# Revit family: Cascata Time Power Floor 20201229 connettori OK
name_source: partatom
category: Attrezzatura meccanica
units: mm (PartAtom-declared; Revit-internal decimal feet)

## family parameters
Basato su piano di lavoro = No
Condiviso = No
Numero OmniClass = 23.75.00.00
Punto di calcolo locali = No
Quota connettore circolare = Usa diametro
Sempre verticale = Sì
Taglio con vuoti quando caricato = No
Tipo di parte = Normale
Titolo OmniClass = Climate Control (HVAC)

## types (23) — shared parameters
Condensate Drain (cascade) = 40 mm  [stored 0.131234 ft]
Date of publishing = 07/01/2021
Design country = Italy
Equilibratore_SX = Sì
Gas Inlet Diameter (cascade) = 165 mm
Manufacturer country = Italy
Manufacturer name = Italtherm S.p.a.
Material main = Metal
Material secondary = Plastic
Product family = Heating
Product group = Thermal unit
Vis.Equil.sx = Sì
zero-valued in all types: Edition number, Prospetto di default

## per-type parameters (varying)
- 340 kW_4 Caldaie: Caldaia_0=Time Power Floor : Time Power Floor 90 K; Caldaia_1=Time Power Floor : Time Power Floor 90 K; Caldaia_2=Time Power Floor : Time Power Floor 90 K; Caldaia_3=Time Power Floor : Time Power Floor 90 K; Diam_flange_equilib=210 mm  [stored 0.688976 ft]; Distanza_ki_INAIL=2308 mm  [stored 7.57218 ft]; Equilibratore_DX=No; Flue outlet (cascade)=200 mm  [stored 0.656168 ft]; Hydronic Return Diameter (cascade)=210 mm  [stored 0.688976 ft]; Hydronic Supply Diameter (cascade)=210 mm  [stored 0.688976 ft]; Maximum heating heat input=340.00 kW; NascTubo=5100 mm  [stored 16.7323 ft]; NumeroCaldaie=4; Numero_Caldaie=4; On_FumiDX_Off_FumiSX=Sì; Qn_MAX=340.00 kW; Scambiatore_DX=No; Scambiatore_SX=No; Sottr=2504 mm  [stored 8.21522 ft]; Vis.Equil.dx=No; Vis.FumiDX=Sì; Vis.FumiSX=No; Vis.Scamb.dx=No; Vis.Scamb.sx=No; Vis.scarico3=Sì; Vis.scarico4=Sì; Visibilità_caldaia_2=Sì; Visibilità_caldaia_3=Sì
- 363 kW_4 Caldaie: Caldaia_0=Time Power Floor : Time Power Floor 90 K; Caldaia_1=Time Power Floor : Time Power Floor 90 K; Caldaia_2=Time Power Floor : Time Power Floor 90 K; Caldaia_3=Time Power Floor : Time Power Floor 115 K; Diam_flange_equilib=210 mm  [stored 0.688976 ft]; Distanza_ki_INAIL=2308 mm  [stored 7.57218 ft]; Equilibratore_DX=Sì; Flue outlet (cascade)=200 mm  [stored 0.656168 ft]; Hydronic Return Diameter (cascade)=210 mm  [stored 0.688976 ft]; Hydronic Supply Diameter (cascade)=210 mm  [stored 0.688976 ft]; Maximum heating heat input=363.00 kW; NascTubo=5100 mm  [stored 16.7323 ft]; NumeroCaldaie=4; Numero_Caldaie=4; On_FumiDX_Off_FumiSX=Sì; Qn_MAX=363.00 kW; Scambiatore_DX=Sì; Scambiatore_SX=Sì; Sottr=2504 mm  [stored 8.21522 ft]; Vis.Equil.dx=Sì; Vis.FumiDX=Sì; Vis.FumiSX=No; Vis.Scamb.dx=Sì; Vis.Scamb.sx=Sì; Vis.scarico3=Sì; Vis.scarico4=Sì; Visibilità_caldaia_2=Sì; Visibilità_caldaia_3=Sì
- 386 kW_4 Caldaie: Caldaia_0=Time Power Floor : Time Power Floor 90 K; Caldaia_1=Time Power Floor : Time Power Floor 90 K; Caldaia_2=Time Power Floor : Time Power Floor 115 K; Caldaia_3=Time Power Floor : Time Power Floor 115 K; Diam_flange_equilib=210 mm  [stored 0.688976 ft]; Distanza_ki_INAIL=2308 mm  [stored 7.57218 ft]; Equilibratore_DX=Sì; Flue outlet (cascade)=200 mm  [stored 0.656168 ft]; Hydronic Return Diameter (cascade)=210 mm  [stored 0.688976 ft]; Hydronic Supply Diameter (cascade)=210 mm  [stored 0.688976 ft]; Maximum heating heat input=386.00 kW; NascTubo=5100 mm  [stored 16.7323 ft]; NumeroCaldaie=4; Numero_Caldaie=4; On_FumiDX_Off_FumiSX=Sì; Qn_MAX=386.00 kW; Scambiatore_DX=Sì; Scambiatore_SX=Sì; Sottr=2504 mm  [stored 8.21522 ft]; Vis.Equil.dx=Sì; Vis.FumiDX=Sì; Vis.FumiSX=No; Vis.Scamb.dx=Sì; Vis.Scamb.sx=Sì; Vis.scarico3=Sì; Vis.scarico4=Sì; Visibilità_caldaia_2=Sì; Visibilità_caldaia_3=Sì
- 405 kW_4 Caldaie: Caldaia_0=Time Power Floor : Time Power Floor 160 K; Caldaia_1=Time Power Floor : Time Power Floor 90 K; Caldaia_2=Time Power Floor : Time Power Floor 90 K; Caldaia_3=Time Power Floor : Time Power Floor 90 K; Diam_flange_equilib=210 mm  [stored 0.688976 ft]; Distanza_ki_INAIL=2308 mm  [stored 7.57218 ft]; Equilibratore_DX=Sì; Flue outlet (cascade)=200 mm  [stored 0.656168 ft]; Hydronic Return Diameter (cascade)=210 mm  [stored 0.688976 ft]; Hydronic Supply Diameter (cascade)=210 mm  [stored 0.688976 ft]; Maximum heating heat input=405.00 kW; NascTubo=5100 mm  [stored 16.7323 ft]; NumeroCaldaie=4; Numero_Caldaie=4; On_FumiDX_Off_FumiSX=Sì; Qn_MAX=405.00 kW; Scambiatore_DX=Sì; Scambiatore_SX=Sì; Sottr=2504 mm  [stored 8.21522 ft]; Vis.Equil.dx=Sì; Vis.FumiDX=Sì; Vis.FumiSX=No; Vis.Scamb.dx=Sì; Vis.Scamb.sx=Sì; Vis.scarico3=Sì; Vis.scarico4=Sì; Visibilità_caldaia_2=Sì; Visibilità_caldaia_3=Sì
- 409 kW_4 Caldaie: Caldaia_0=Time Power Floor : Time Power Floor 115 K; Caldaia_1=Time Power Floor : Time Power Floor 115 K; Caldaia_2=Time Power Floor : Time Power Floor 115 K; Caldaia_3=Time Power Floor : Time Power Floor 90 K; Diam_flange_equilib=210 mm  [stored 0.688976 ft]; Distanza_ki_INAIL=2308 mm  [stored 7.57218 ft]; Equilibratore_DX=Sì; Flue outlet (cascade)=200 mm  [stored 0.656168 ft]; Hydronic Return Diameter (cascade)=210 mm  [stored 0.688976 ft]; Hydronic Supply Diameter (cascade)=210 mm  [stored 0.688976 ft]; Maximum heating heat input=409.00 kW; NascTubo=5100 mm  [stored 16.7323 ft]; NumeroCaldaie=4; Numero_Caldaie=4; On_FumiDX_Off_FumiSX=Sì; Qn_MAX=409.00 kW; Scambiatore_DX=Sì; Scambiatore_SX=Sì; Sottr=2504 mm  [stored 8.21522 ft]; Vis.Equil.dx=Sì; Vis.FumiDX=Sì; Vis.FumiSX=No; Vis.Scamb.dx=Sì; Vis.Scamb.sx=Sì; Vis.scarico3=Sì; Vis.scarico4=Sì; Visibilità_caldaia_2=Sì; Visibilità_caldaia_3=Sì
- 428 kW_4 Caldaie: Caldaia_0=Time Power Floor : Time Power Floor 160 K; Caldaia_1=Time Power Floor : Time Power Floor 115 K; Caldaia_2=Time Power Floor : Time Power Floor 90 K; Caldaia_3=Time Power Floor : Time Power Floor 90 K; Diam_flange_equilib=210 mm  [stored 0.688976 ft]; Distanza_ki_INAIL=2308 mm  [stored 7.57218 ft]; Equilibratore_DX=Sì; Flue outlet (cascade)=200 mm  [stored 0.656168 ft]; Hydronic Return Diameter (cascade)=210 mm  [stored 0.688976 ft]; Hydronic Supply Diameter (cascade)=210 mm  [stored 0.688976 ft]; Maximum heating heat input=428.00 kW; NascTubo=5100 mm  [stored 16.7323 ft]; NumeroCaldaie=4; Numero_Caldaie=4; On_FumiDX_Off_FumiSX=Sì; Qn_MAX=428.00 kW; Scambiatore_DX=Sì; Scambiatore_SX=Sì; Sottr=2504 mm  [stored 8.21522 ft]; Vis.Equil.dx=Sì; Vis.FumiDX=Sì; Vis.FumiSX=No; Vis.Scamb.dx=Sì; Vis.Scamb.sx=Sì; Vis.scarico3=Sì; Vis.scarico4=Sì; Visibilità_caldaia_2=Sì; Visibilità_caldaia_3=Sì
- 432 kW_4 Caldaie: Caldaia_0=Time Power Floor : Time Power Floor 115 K; Caldaia_1=Time Power Floor : Time Power Floor 115 K; Caldaia_2=Time Power Floor : Time Power Floor 115 K; Caldaia_3=Time Power Floor : Time Power Floor 115 K; Diam_flange_equilib=210 mm  [stored 0.688976 ft]; Distanza_ki_INAIL=2308 mm  [stored 7.57218 ft]; Equilibratore_DX=Sì; Flue outlet (cascade)=200 mm  [stored 0.656168 ft]; Hydronic Return Diameter (cascade)=210 mm  [stored 0.688976 ft]; Hydronic Supply Diameter (cascade)=210 mm  [stored 0.688976 ft]; Maximum heating heat input=432.00 kW; NascTubo=5100 mm  [stored 16.7323 ft]; NumeroCaldaie=4; Numero_Caldaie=4; On_FumiDX_Off_FumiSX=Sì; Qn_MAX=432.00 kW; Scambiatore_DX=Sì; Scambiatore_SX=Sì; Sottr=2504 mm  [stored 8.21522 ft]; Vis.Equil.dx=Sì; Vis.FumiDX=Sì; Vis.FumiSX=No; Vis.Scamb.dx=Sì; Vis.Scamb.sx=Sì; Vis.scarico3=Sì; Vis.scarico4=Sì; Visibilità_caldaia_2=Sì; Visibilità_caldaia_3=Sì
- 255 kW_3 Caldaie: Caldaia_0=Time Power Floor : Time Power Floor 90 K; Caldaia_1=Time Power Floor : Time Power Floor 90 K; Caldaia_2=Time Power Floor : Time Power Floor 90 K; Caldaia_3=Time Power Floor : Nessuna; Diam_flange_equilib=185 mm  [stored 0.606955 ft]; Distanza_ki_INAIL=1726 mm; Equilibratore_DX=Sì; Flue outlet (cascade)=160 mm  [stored 0.524934 ft]; Hydronic Return Diameter (cascade)=185 mm  [stored 0.606955 ft]; Hydronic Supply Diameter (cascade)=185 mm  [stored 0.606955 ft]; Maximum heating heat input=255.00 kW; NascTubo=4400 mm; NumeroCaldaie=3; Numero_Caldaie=3; On_FumiDX_Off_FumiSX=Sì; Qn_MAX=255.00 kW; Scambiatore_DX=Sì; Scambiatore_SX=Sì; Sottr=1922 mm; Vis.Equil.dx=Sì; Vis.FumiDX=Sì; Vis.FumiSX=No; Vis.Scamb.dx=Sì; Vis.Scamb.sx=Sì; Vis.scarico3=Sì; Vis.scarico4=No; Visibilità_caldaia_2=Sì; Visibilità_caldaia_3=No
- 278 kW_3 Caldaie: Caldaia_0=Time Power Floor : Time Power Floor 90 K; Caldaia_1=Time Power Floor : Time Power Floor 90 K; Caldaia_2=Time Power Floor : Time Power Floor 115 K; Caldaia_3=Time Power Floor : Nessuna; Diam_flange_equilib=185 mm  [stored 0.606955 ft]; Distanza_ki_INAIL=1726 mm; Equilibratore_DX=Sì; Flue outlet (cascade)=200 mm  [stored 0.656168 ft]; Hydronic Return Diameter (cascade)=185 mm  [stored 0.606955 ft]; Hydronic Supply Diameter (cascade)=185 mm  [stored 0.606955 ft]; Maximum heating heat input=278.00 kW; NascTubo=4400 mm; NumeroCaldaie=3; Numero_Caldaie=3; On_FumiDX_Off_FumiSX=Sì; Qn_MAX=278.00 kW; Scambiatore_DX=Sì; Scambiatore_SX=Sì; Sottr=1922 mm; Vis.Equil.dx=Sì; Vis.FumiDX=Sì; Vis.FumiSX=No; Vis.Scamb.dx=Sì; Vis.Scamb.sx=Sì; Vis.scarico3=Sì; Vis.scarico4=No; Visibilità_caldaia_2=Sì; Visibilità_caldaia_3=No
- 301 kW_3 Caldaie: Caldaia_0=Time Power Floor : Time Power Floor 90 K; Caldaia_1=Time Power Floor : Time Power Floor 115 K; Caldaia_2=Time Power Floor : Time Power Floor 115 K; Caldaia_3=Time Power Floor : Nessuna; Diam_flange_equilib=210 mm  [stored 0.688976 ft]; Distanza_ki_INAIL=1726 mm; Equilibratore_DX=Sì; Flue outlet (cascade)=200 mm  [stored 0.656168 ft]; Hydronic Return Diameter (cascade)=210 mm  [stored 0.688976 ft]; Hydronic Supply Diameter (cascade)=210 mm  [stored 0.688976 ft]; Maximum heating heat input=301.00 kW; NascTubo=4400 mm; NumeroCaldaie=3; Numero_Caldaie=3; On_FumiDX_Off_FumiSX=Sì; Qn_MAX=301.00 kW; Scambiatore_DX=Sì; Scambiatore_SX=Sì; Sottr=1922 mm; Vis.Equil.dx=Sì; Vis.FumiDX=Sì; Vis.FumiSX=No; Vis.Scamb.dx=Sì; Vis.Scamb.sx=Sì; Vis.scarico3=Sì; Vis.scarico4=No; Visibilità_caldaia_2=Sì; Visibilità_caldaia_3=No
- 320 kW_3 Caldaie: Caldaia_0=Time Power Floor : Time Power Floor 160 K; Caldaia_1=Time Power Floor : Time Power Floor 90 K; Caldaia_2=Time Power Floor : Time Power Floor 90 K; Caldaia_3=Time Power Floor : Nessuna; Diam_flange_equilib=210 mm  [stored 0.688976 ft]; Distanza_ki_INAIL=1726 mm; Equilibratore_DX=Sì; Flue outlet (cascade)=200 mm  [stored 0.656168 ft]; Hydronic Return Diameter (cascade)=210 mm  [stored 0.688976 ft]; Hydronic Supply Diameter (cascade)=210 mm  [stored 0.688976 ft]; Maximum heating heat input=320.00 kW; NascTubo=4400 mm; NumeroCaldaie=3; Numero_Caldaie=3; On_FumiDX_Off_FumiSX=Sì; Qn_MAX=320.00 kW; Scambiatore_DX=Sì; Scambiatore_SX=Sì; Sottr=1922 mm; Vis.Equil.dx=Sì; Vis.FumiDX=Sì; Vis.FumiSX=No; Vis.Scamb.dx=Sì; Vis.Scamb.sx=Sì; Vis.scarico3=Sì; Vis.scarico4=No; Visibilità_caldaia_2=Sì; Visibilità_caldaia_3=No
- 324 kW_3 Caldaie: Caldaia_0=Time Power Floor : Time Power Floor 115 K; Caldaia_1=Time Power Floor : Time Power Floor 115 K; Caldaia_2=Time Power Floor : Time Power Floor 115 K; Caldaia_3=Time Power Floor : Nessuna; Diam_flange_equilib=210 mm  [stored 0.688976 ft]; Distanza_ki_INAIL=1726 mm; Equilibratore_DX=Sì; Flue outlet (cascade)=200 mm  [stored 0.656168 ft]; Hydronic Return Diameter (cascade)=210 mm  [stored 0.688976 ft]; Hydronic Supply Diameter (cascade)=210 mm  [stored 0.688976 ft]; Maximum heating heat input=324.00 kW; NascTubo=4400 mm; NumeroCaldaie=3; Numero_Caldaie=3; On_FumiDX_Off_FumiSX=Sì; Qn_MAX=324.00 kW; Scambiatore_DX=Sì; Scambiatore_SX=Sì; Sottr=1922 mm; Vis.Equil.dx=Sì; Vis.FumiDX=Sì; Vis.FumiSX=No; Vis.Scamb.dx=Sì; Vis.Scamb.sx=Sì; Vis.scarico3=Sì; Vis.scarico4=No; Visibilità_caldaia_2=Sì; Visibilità_caldaia_3=No
- 343 kW_3 Caldaie: Caldaia_0=Time Power Floor : Time Power Floor 160 K; Caldaia_1=Time Power Floor : Time Power Floor 115 K; Caldaia_2=Time Power Floor : Time Power Floor 90 K; Caldaia_3=Time Power Floor : Nessuna; Diam_flange_equilib=210 mm  [stored 0.688976 ft]; Distanza_ki_INAIL=1726 mm; Equilibratore_DX=Sì; Flue outlet (cascade)=200 mm  [stored 0.656168 ft]; Hydronic Return Diameter (cascade)=210 mm  [stored 0.688976 ft]; Hydronic Supply Diameter (cascade)=210 mm  [stored 0.688976 ft]; Maximum heating heat input=343.00 kW; NascTubo=4400 mm; NumeroCaldaie=3; Numero_Caldaie=3; On_FumiDX_Off_FumiSX=Sì; Qn_MAX=343.00 kW; Scambiatore_DX=Sì; Scambiatore_SX=Sì; Sottr=1922 mm; Vis.Equil.dx=Sì; Vis.FumiDX=Sì; Vis.FumiSX=No; Vis.Scamb.dx=Sì; Vis.Scamb.sx=Sì; Vis.scarico3=Sì; Vis.scarico4=No; Visibilità_caldaia_2=Sì; Visibilità_caldaia_3=No
- 366 kW_3 Caldaie: Caldaia_0=Time Power Floor : Time Power Floor 160 K; Caldaia_1=Time Power Floor : Time Power Floor 115 K; Caldaia_2=Time Power Floor : Time Power Floor 115 K; Caldaia_3=Time Power Floor : Nessuna; Diam_flange_equilib=185 mm  [stored 0.606955 ft]; Distanza_ki_INAIL=1726 mm; Equilibratore_DX=Sì; Flue outlet (cascade)=125 mm  [stored 0.410105 ft]; Hydronic Return Diameter (cascade)=185 mm  [stored 0.606955 ft]; Hydronic Supply Diameter (cascade)=185 mm  [stored 0.606955 ft]; Maximum heating heat input=0.00 kW; NascTubo=4400 mm; NumeroCaldaie=3; Numero_Caldaie=3; On_FumiDX_Off_FumiSX=Sì; Qn_MAX=0.00 kW; Scambiatore_DX=Sì; Scambiatore_SX=Sì; Sottr=1922 mm; Vis.Equil.dx=Sì; Vis.FumiDX=Sì; Vis.FumiSX=No; Vis.Scamb.dx=Sì; Vis.Scamb.sx=Sì; Vis.scarico3=Sì; Vis.scarico4=No; Visibilità_caldaia_2=Sì; Visibilità_caldaia_3=No
- 385 kW_3 Caldaie: Caldaia_0=Time Power Floor : Time Power Floor 160 K; Caldaia_1=Time Power Floor : Time Power Floor 160 K; Caldaia_2=Time Power Floor : Time Power Floor 90 K; Caldaia_3=Time Power Floor : Nessuna; Diam_flange_equilib=210 mm  [stored 0.688976 ft]; Distanza_ki_INAIL=1726 mm; Equilibratore_DX=Sì; Flue outlet (cascade)=200 mm  [stored 0.656168 ft]; Hydronic Return Diameter (cascade)=210 mm  [stored 0.688976 ft]; Hydronic Supply Diameter (cascade)=210 mm  [stored 0.688976 ft]; Maximum heating heat input=385.00 kW; NascTubo=4400 mm; NumeroCaldaie=3; Numero_Caldaie=3; On_FumiDX_Off_FumiSX=Sì; Qn_MAX=385.00 kW; Scambiatore_DX=Sì; Scambiatore_SX=Sì; Sottr=1922 mm; Vis.Equil.dx=Sì; Vis.FumiDX=Sì; Vis.FumiSX=No; Vis.Scamb.dx=Sì; Vis.Scamb.sx=Sì; Vis.scarico3=Sì; Vis.scarico4=No; Visibilità_caldaia_2=Sì; Visibilità_caldaia_3=No
- 408 kW_3 Caldaie: Caldaia_0=Time Power Floor : Time Power Floor 160 K; Caldaia_1=Time Power Floor : Time Power Floor 160 K; Caldaia_2=Time Power Floor : Time Power Floor 115 K; Caldaia_3=Time Power Floor : Nessuna; Diam_flange_equilib=210 mm  [stored 0.688976 ft]; Distanza_ki_INAIL=1726 mm; Equilibratore_DX=Sì; Flue outlet (cascade)=200 mm  [stored 0.656168 ft]; Hydronic Return Diameter (cascade)=210 mm  [stored 0.688976 ft]; Hydronic Supply Diameter (cascade)=210 mm  [stored 0.688976 ft]; Maximum heating heat input=408.00 kW; NascTubo=4400 mm; NumeroCaldaie=3; Numero_Caldaie=3; On_FumiDX_Off_FumiSX=Sì; Qn_MAX=408.00 kW; Scambiatore_DX=Sì; Scambiatore_SX=Sì; Sottr=1922 mm; Vis.Equil.dx=Sì; Vis.FumiDX=Sì; Vis.FumiSX=No; Vis.Scamb.dx=Sì; Vis.Scamb.sx=Sì; Vis.scarico3=Sì; Vis.scarico4=No; Visibilità_caldaia_2=Sì; Visibilità_caldaia_3=No
- 450 kW_3 Caldaie: Caldaia_0=Time Power Floor : Time Power Floor 160 K; Caldaia_1=Time Power Floor : Time Power Floor 160 K; Caldaia_2=Time Power Floor : Time Power Floor 160 K; Caldaia_3=Time Power Floor : Nessuna; Diam_flange_equilib=210 mm  [stored 0.688976 ft]; Distanza_ki_INAIL=1726 mm; Equilibratore_DX=Sì; Flue outlet (cascade)=200 mm  [stored 0.656168 ft]; Hydronic Return Diameter (cascade)=210 mm  [stored 0.688976 ft]; Hydronic Supply Diameter (cascade)=210 mm  [stored 0.688976 ft]; Maximum heating heat input=450.00 kW; NascTubo=4400 mm; NumeroCaldaie=3; Numero_Caldaie=3; On_FumiDX_Off_FumiSX=Sì; Qn_MAX=450.00 kW; Scambiatore_DX=Sì; Scambiatore_SX=Sì; Sottr=1922 mm; Vis.Equil.dx=Sì; Vis.FumiDX=Sì; Vis.FumiSX=No; Vis.Scamb.dx=Sì; Vis.Scamb.sx=Sì; Vis.scarico3=Sì; Vis.scarico4=No; Visibilità_caldaia_2=Sì; Visibilità_caldaia_3=No
- 170 kW_2 Caldaie: Caldaia_0=Time Power Floor : Time Power Floor 90 K; Caldaia_1=Time Power Floor : Time Power Floor 90 K; Caldaia_2=Time Power Floor : Nessuna; Caldaia_3=Time Power Floor : Nessuna; Diam_flange_equilib=185 mm  [stored 0.606955 ft]; Distanza_ki_INAIL=1144 mm; Equilibratore_DX=Sì; Flue outlet (cascade)=160 mm  [stored 0.524934 ft]; Hydronic Return Diameter (cascade)=185 mm  [stored 0.606955 ft]; Hydronic Supply Diameter (cascade)=185 mm  [stored 0.606955 ft]; Maximum heating heat input=170.00 kW; NascTubo=3700 mm  [stored 12.1391 ft]; NumeroCaldaie=2; Numero_Caldaie=2; On_FumiDX_Off_FumiSX=No; Qn_MAX=170.00 kW; Scambiatore_DX=Sì; Scambiatore_SX=Sì; Sottr=1340 mm; Vis.Equil.dx=Sì; Vis.FumiDX=No; Vis.FumiSX=Sì; Vis.Scamb.dx=Sì; Vis.Scamb.sx=Sì; Vis.scarico3=No; Vis.scarico4=No; Visibilità_caldaia_2=No; Visibilità_caldaia_3=No
- 193 kW_2 Caldaie: Caldaia_0=Time Power Floor : Time Power Floor 90 K; Caldaia_1=Time Power Floor : Time Power Floor 115 K; Caldaia_2=Time Power Floor : Nessuna; Caldaia_3=Time Power Floor : Nessuna; Diam_flange_equilib=185 mm  [stored 0.606955 ft]; Distanza_ki_INAIL=1144 mm; Equilibratore_DX=Sì; Flue outlet (cascade)=160 mm  [stored 0.524934 ft]; Hydronic Return Diameter (cascade)=185 mm  [stored 0.606955 ft]; Hydronic Supply Diameter (cascade)=185 mm  [stored 0.606955 ft]; Maximum heating heat input=193.00 kW; NascTubo=3700 mm  [stored 12.1391 ft]; NumeroCaldaie=2; Numero_Caldaie=2; On_FumiDX_Off_FumiSX=Sì; Qn_MAX=193.00 kW; Scambiatore_DX=Sì; Scambiatore_SX=Sì; Sottr=1340 mm; Vis.Equil.dx=Sì; Vis.FumiDX=Sì; Vis.FumiSX=No; Vis.Scamb.dx=Sì; Vis.Scamb.sx=Sì; Vis.scarico3=No; Vis.scarico4=No; Visibilità_caldaia_2=No; Visibilità_caldaia_3=No
- 216 kW_2 Caldaie: Caldaia_0=Time Power Floor : Time Power Floor 115 K; Caldaia_1=Time Power Floor : Time Power Floor 115 K; Caldaia_2=Time Power Floor : Nessuna; Caldaia_3=Time Power Floor : Nessuna; Diam_flange_equilib=185 mm  [stored 0.606955 ft]; Distanza_ki_INAIL=1144 mm; Equilibratore_DX=Sì; Flue outlet (cascade)=160 mm  [stored 0.524934 ft]; Hydronic Return Diameter (cascade)=185 mm  [stored 0.606955 ft]; Hydronic Supply Diameter (cascade)=185 mm  [stored 0.606955 ft]; Maximum heating heat input=216.00 kW; NascTubo=3700 mm  [stored 12.1391 ft]; NumeroCaldaie=2; Numero_Caldaie=2; On_FumiDX_Off_FumiSX=Sì; Qn_MAX=216.00 kW; Scambiatore_DX=Sì; Scambiatore_SX=Sì; Sottr=1340 mm; Vis.Equil.dx=Sì; Vis.FumiDX=Sì; Vis.FumiSX=No; Vis.Scamb.dx=Sì; Vis.Scamb.sx=Sì; Vis.scarico3=No; Vis.scarico4=No; Visibilità_caldaia_2=No; Visibilità_caldaia_3=No
- 235 kW_2 Caldaie: Caldaia_0=Time Power Floor : Time Power Floor 160 K; Caldaia_1=Time Power Floor : Time Power Floor 90 K; Caldaia_2=Time Power Floor : Nessuna; Caldaia_3=Time Power Floor : Nessuna; Diam_flange_equilib=185 mm  [stored 0.606955 ft]; Distanza_ki_INAIL=1144 mm; Equilibratore_DX=Sì; Flue outlet (cascade)=160 mm  [stored 0.524934 ft]; Hydronic Return Diameter (cascade)=185 mm  [stored 0.606955 ft]; Hydronic Supply Diameter (cascade)=185 mm  [stored 0.606955 ft]; Maximum heating heat input=235.00 kW; NascTubo=3700 mm  [stored 12.1391 ft]; NumeroCaldaie=2; Numero_Caldaie=2; On_FumiDX_Off_FumiSX=Sì; Qn_MAX=235.00 kW; Scambiatore_DX=Sì; Scambiatore_SX=Sì; Sottr=1340 mm; Vis.Equil.dx=Sì; Vis.FumiDX=Sì; Vis.FumiSX=No; Vis.Scamb.dx=Sì; Vis.Scamb.sx=Sì; Vis.scarico3=No; Vis.scarico4=No; Visibilità_caldaia_2=No; Visibilità_caldaia_3=No
- 258 kW_2 Caldaie: Caldaia_0=Time Power Floor : Time Power Floor 160 K; Caldaia_1=Time Power Floor : Time Power Floor 115 K; Caldaia_2=Time Power Floor : Nessuna; Caldaia_3=Time Power Floor : Nessuna; Diam_flange_equilib=185 mm  [stored 0.606955 ft]; Distanza_ki_INAIL=1144 mm; Equilibratore_DX=Sì; Flue outlet (cascade)=160 mm  [stored 0.524934 ft]; Hydronic Return Diameter (cascade)=185 mm  [stored 0.606955 ft]; Hydronic Supply Diameter (cascade)=185 mm  [stored 0.606955 ft]; Maximum heating heat input=258.00 kW; NascTubo=3700 mm  [stored 12.1391 ft]; NumeroCaldaie=2; Numero_Caldaie=2; On_FumiDX_Off_FumiSX=Sì; Qn_MAX=258.00 kW; Scambiatore_DX=Sì; Scambiatore_SX=Sì; Sottr=1340 mm; Vis.Equil.dx=Sì; Vis.FumiDX=Sì; Vis.FumiSX=No; Vis.Scamb.dx=Sì; Vis.Scamb.sx=Sì; Vis.scarico3=No; Vis.scarico4=No; Visibilità_caldaia_2=No; Visibilità_caldaia_3=No
- 300 kW_2 Caldaie: Caldaia_0=Time Power Floor : Time Power Floor 160 K; Caldaia_1=Time Power Floor : Time Power Floor 160 K; Caldaia_2=Time Power Floor : Nessuna; Caldaia_3=Time Power Floor : Nessuna; Diam_flange_equilib=210 mm  [stored 0.688976 ft]; Distanza_ki_INAIL=1144 mm; Equilibratore_DX=Sì; Flue outlet (cascade)=200 mm  [stored 0.656168 ft]; Hydronic Return Diameter (cascade)=210 mm  [stored 0.688976 ft]; Hydronic Supply Diameter (cascade)=210 mm  [stored 0.688976 ft]; Maximum heating heat input=300.00 kW; NascTubo=3700 mm  [stored 12.1391 ft]; NumeroCaldaie=2; Numero_Caldaie=2; On_FumiDX_Off_FumiSX=Sì; Qn_MAX=300.00 kW; Scambiatore_DX=Sì; Scambiatore_SX=Sì; Sottr=1340 mm; Vis.Equil.dx=Sì; Vis.FumiDX=Sì; Vis.FumiSX=No; Vis.Scamb.dx=Sì; Vis.Scamb.sx=Sì; Vis.scarico3=No; Vis.scarico4=No; Visibilità_caldaia_2=No; Visibilità_caldaia_3=No

note: [stored X ft] marks values corroborated as IEEE doubles in the binary element streams (Revit-internal decimal feet)
